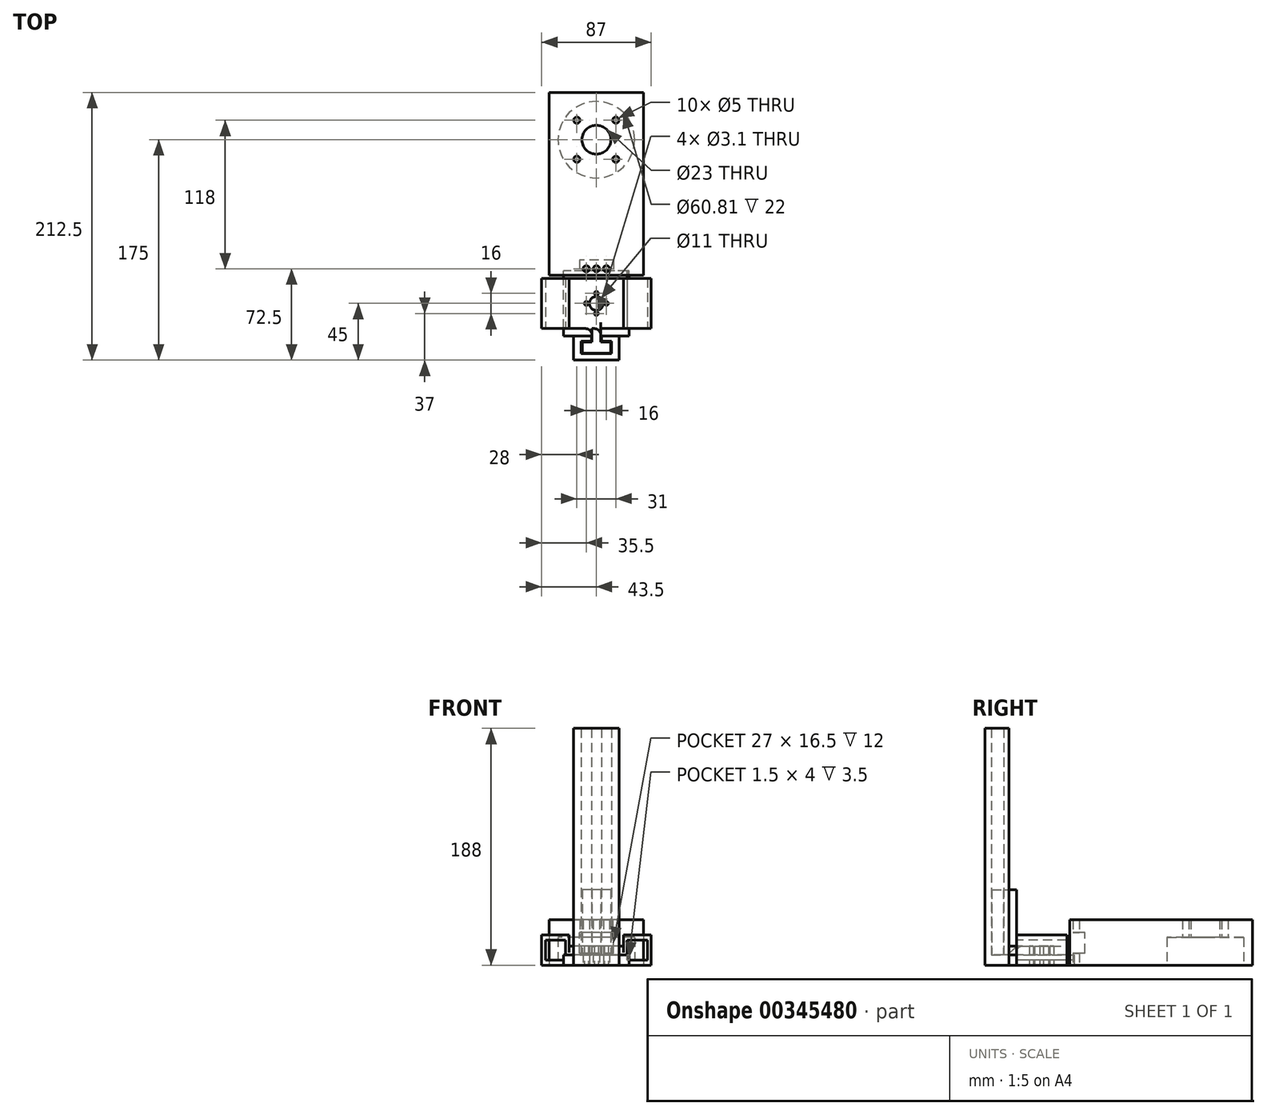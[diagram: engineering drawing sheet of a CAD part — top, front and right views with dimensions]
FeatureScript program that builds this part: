
annotation { "Feature Type Name" : "Feature", "Feature Type Description" : "" }
export const myFeature = defineFeature(function(context is Context, id is Id, definition is map)
    precondition{}
    {
        {
            var Q0;
            Q0=qCreatedBy(makeId("Top.planeOp"),FACE);
            var sketch = newSketch(context, id + "F0", { "sketchPlane" : qUnion([Q0])});
            skLineSegment(sketch, "E0.bottom", {"start": v(18, -10) * mm, "end": v(-18, -10) * mm});
            skLineSegment(sketch, "E0.top", {"start": v(18, 10) * mm, "end": v(4, 10) * mm});
            skLineSegment(sketch, "E0.left", {"start": v(18, -10) * mm, "end": v(18, 10) * mm});
            skLineSegment(sketch, "E0.right", {"start": v(-18, -10) * mm, "end": v(-18, 10) * mm});
            skPoint(sketch, "E0.middle", {"position": v(0, 0) * mm});
            skLineSegment(sketch, "E1.bottom", {"start": v(12, -5) * mm, "end": v(-12, -5) * mm});
            skLineSegment(sketch, "E1.top", {"start": v(12, 5) * mm, "end": v(4, 5) * mm});
            skLineSegment(sketch, "E1.left", {"start": v(12, -5) * mm, "end": v(12, 5) * mm});
            skLineSegment(sketch, "E1.right", {"start": v(-12, -5) * mm, "end": v(-12, 5) * mm});
            skPoint(sketch, "E2", {"position": v(-4, 10) * mm});
            skPoint(sketch, "E3.MirrorP", {"position": v(4, 10) * mm});
            skLineSegment(sketch, "E4", {"start": v(-4, 10) * mm, "end": v(-4, 5) * mm});
            skLineSegment(sketch, "E5", {"start": v(4, 10) * mm, "end": v(4, 5) * mm});
            skLineSegment(sketch, "E6.trimOffspring", {"start": v(-4, 10) * mm, "end": v(-18, 10) * mm});
            skLineSegment(sketch, "E7.trimOffspring", {"start": v(-4, 5) * mm, "end": v(-12, 5) * mm});
            skLineSegment(sketch, "E8.bottom", {"start": v(15.5, 19.5) * mm, "end": v(-15.5, 19.5) * mm, "construction": true});
            skLineSegment(sketch, "E8.top", {"start": v(15.5, 50.5) * mm, "end": v(-15.5, 50.5) * mm, "construction": true});
            skLineSegment(sketch, "E8.left", {"start": v(15.5, 19.5) * mm, "end": v(15.5, 50.5) * mm, "construction": true});
            skLineSegment(sketch, "E8.right", {"start": v(-15.5, 19.5) * mm, "end": v(-15.5, 50.5) * mm, "construction": true});
            skPoint(sketch, "E8.middle", {"position": v(0, 35) * mm});
            skCircle(sketch, "E9", {"center": v(15.5, 50.5) * mm, "radius": 2.5 * mm});
            skCircle(sketch, "E10", {"center": v(15.5, 19.5) * mm, "radius": 2.5 * mm});
            skCircle(sketch, "E11", {"center": v(-15.5, 19.5) * mm, "radius": 2.5 * mm});
            skCircle(sketch, "E12", {"center": v(-15.5, 50.5) * mm, "radius": 2.5 * mm});
            skLineSegment(sketch, "E13.bottom", {"start": v(26, 9) * mm, "end": v(-26, 9) * mm});
            skLineSegment(sketch, "E13.top", {"start": v(26, 61) * mm, "end": v(-26, 61) * mm});
            skLineSegment(sketch, "E13.left", {"start": v(26, 9) * mm, "end": v(26, 61) * mm});
            skLineSegment(sketch, "E13.right", {"start": v(-26, 9) * mm, "end": v(-26, 61) * mm});
            skCircle(sketch, "E14", {"center": v(0, 35) * mm, "radius": 11.5 * mm});
            skSolve(sketch);
        }
        {
            var Q0;
            Q0=makeQuery(id+"F0.imprint","IMPRINT",FACE,{"disambiguationData":[TD([[makeQuery(id+"F0.imprint","IMPRINT",EDGE,{"derivedFrom":sQuery(id+"F0.wireOp",EDGE,"E0.bottom")}),-1.0]])]});
            extrude(context, id + "F1", {"entities" : qUnion([Q0]), "depth" : 10 * mm});
        }
        {
            var Q0;
            Q0=qCreatedBy(makeId("Top.planeOp"),FACE);
            var sketch = newSketch(context, id + "F2", { "sketchPlane" : qUnion([Q0])});
            skLineSegment(sketch, "E15.bottom", {"start": v(11.25, -4.5) * mm, "end": v(-11.25, -4.5) * mm});
            skLineSegment(sketch, "E15.top", {"start": v(11.25, 4.5) * mm, "end": v(3.5, 4.5) * mm});
            skLineSegment(sketch, "E15.left", {"start": v(11.25, -4.5) * mm, "end": v(11.25, 4.5) * mm});
            skLineSegment(sketch, "E15.right", {"start": v(-11.25, -4.5) * mm, "end": v(-11.25, 4.5) * mm});
            skPoint(sketch, "E15.middle", {"position": v(0, 0) * mm});
            skLineSegment(sketch, "E16.top", {"start": v(3.5, 24.5) * mm, "end": v(-3.5, 24.5) * mm});
            skLineSegment(sketch, "E16.left", {"start": v(3.5, 4.5) * mm, "end": v(3.5, 24.5) * mm});
            skLineSegment(sketch, "E16.right", {"start": v(-3.5, 4.5) * mm, "end": v(-3.5, 24.5) * mm});
            skPoint(sketch, "E16.middle", {"position": v(0, 14.5) * mm});
            skLineSegment(sketch, "E17.trimOffspring", {"start": v(-3.5, 4.5) * mm, "end": v(-11.25, 4.5) * mm});
            skPoint(sketch, "E18.0", {"position": v(0, 35) * mm});
            skCircle(sketch, "E19", {"center": v(0, 35) * mm, "radius": 5.5 * mm});
            skCircle(sketch, "E20", {"center": v(0, 35) * mm, "radius": 8 * mm, "construction": true});
            skCircle(sketch, "E21", {"center": v(0, 43) * mm, "radius": 1.55 * mm});
            skCircle(sketch, "E22.1.0", {"center": v(-8, 35) * mm, "radius": 1.55 * mm});
            skCircle(sketch, "E22.2.0", {"center": v(0, 27) * mm, "radius": 1.55 * mm});
            skCircle(sketch, "E22.3.0", {"center": v(8, 35) * mm, "radius": 1.55 * mm});
            skLineSegment(sketch, "E23.bottom", {"start": v(21.5, 15) * mm, "end": v(-21.5, 15) * mm});
            skLineSegment(sketch, "E23.top", {"start": v(21.5, 55) * mm, "end": v(-21.5, 55) * mm});
            skLineSegment(sketch, "E23.left", {"start": v(21.5, 15) * mm, "end": v(21.5, 55) * mm});
            skLineSegment(sketch, "E23.right", {"start": v(-21.5, 15) * mm, "end": v(-21.5, 55) * mm});
            skLineSegment(sketch, "E24.bottom", {"start": v(-21.5, 55) * mm, "end": v(21.5, 55) * mm});
            skPoint(sketch, "E25.orphan", {"position": v(-21.5, 60) * mm});
            skPoint(sketch, "E26.center.orphan", {"position": v(-8, 60) * mm});
            skPoint(sketch, "E27.center.orphan", {"position": v(8, 60) * mm});
            skPoint(sketch, "E28.center.orphan", {"position": v(0, 60) * mm});
            skPoint(sketch, "E29.orphan", {"position": v(21.5, 60) * mm});
            skPoint(sketch, "E24.top.start.orphan", {"position": v(-21.5, 65) * mm});
            skPoint(sketch, "E30.orphan", {"position": v(21.5, 65) * mm});
            skLineSegment(sketch, "E31.bottom", {"start": v(21.5, 15) * mm, "end": v(43.5, 15) * mm});
            skLineSegment(sketch, "E31.top", {"start": v(21.5, 55) * mm, "end": v(43.5, 55) * mm});
            skLineSegment(sketch, "E31.right", {"start": v(43.5, 15) * mm, "end": v(43.5, 55) * mm});
            skLineSegment(sketch, "E32.MirrorCS", {"start": v(-43.5, 15) * mm, "end": v(-43.5, 55) * mm});
            skLineSegment(sketch, "E33.MirrorCS", {"start": v(-21.5, 15) * mm, "end": v(-43.5, 15) * mm});
            skLineSegment(sketch, "E34.MirrorCS", {"start": v(-21.5, 55) * mm, "end": v(-43.5, 55) * mm});
            skSolve(sketch);
        }
        {
            var Q0;
            Q0=makeQuery(id+"F2.imprint","IMPRINT",FACE,{"disambiguationData":[TD([[makeQuery(id+"F2.imprint","IMPRINT",EDGE,{"derivedFrom":sQuery(id+"F2.wireOp",EDGE,"E15.bottom")}),-1.0]])]});
            extrude(context, id + "F3", {"entities" : qUnion([Q0]), "depth" : 5 * mm});
        }
        {
            var Q0;
            {var subQ5=sQuery(id+"F0.wireOp",EDGE,"E0.bottom");Q0=makeQuery(id+"F0.imprint","IMPRINT",FACE,{"disambiguationData":[TD([[makeQuery(id+"F0.imprint","IMPRINT",EDGE,{"derivedFrom":subQ5}),-1.0]])]});}
            extrude(context, id + "F4", {"entities" : qUnion([Q0]), "depth" : 188 * mm});
        }
        {
            var Q0;
            {var subQ1=sQuery(id+"F0.wireOp",EDGE,"E0.top");Q0=makeQuery(id+"F0.imprint","IMPRINT",FACE,{"disambiguationData":[TD([[makeQuery(id+"F0.imprint","IMPRINT",EDGE,{"derivedFrom":subQ1}),-1.0]])]});}
            extrude(context, id + "F5", {"entities" : qUnion([Q0]), "operationType" : NewBodyOperationType.ADD, "depth" : 8 * mm});
        }
        {
            var Q0;
            Q0=makeQuery(id+"F5.opExtrude","SWEPT_BODY",BODY,{"disambiguationData":[OSD([sQuery(id+"F0.wireOp",EDGE,"E0.top"),sQuery(id+"F0.wireOp",EDGE,"E0.left"),sQuery(id+"F0.wireOp",EDGE,"E0.right"),sQuery(id+"F0.wireOp",EDGE,"E4"),sQuery(id+"F0.wireOp",EDGE,"E5"),sQuery(id+"F0.wireOp",EDGE,"E6.trimOffspring"),sQuery(id+"F0.wireOp",EDGE,"E9"),sQuery(id+"F0.wireOp",EDGE,"E10"),sQuery(id+"F0.wireOp",EDGE,"E11"),sQuery(id+"F0.wireOp",EDGE,"E12"),sQuery(id+"F0.wireOp",EDGE,"E13.bottom"),sQuery(id+"F0.wireOp",EDGE,"E13.top"),sQuery(id+"F0.wireOp",EDGE,"E13.left"),sQuery(id+"F0.wireOp",EDGE,"E13.right"),sQuery(id+"F0.wireOp",EDGE,"E14")])]});
            deleteBodies(context, id + "F6", {"entities" : qUnion([Q0])});
        }
        {
            var Q0;
            Q0=makeQuery(id+"F0.imprint","IMPRINT",FACE,{"disambiguationData":[TD([[makeQuery(id+"F0.imprint","IMPRINT",EDGE,{"derivedFrom":sQuery(id+"F0.wireOp",EDGE,"E1.bottom")}),-1.0]])]});
            var Q1;
            {var subQ1=sQuery(id+"F0.wireOp",EDGE,"E0.top");Q1=makeQuery(id+"F0.imprint","IMPRINT",FACE,{"disambiguationData":[TD([[makeQuery(id+"F0.imprint","IMPRINT",EDGE,{"derivedFrom":subQ1}),-1.0]])]});}
            var Q2;
            {var subQ5=sQuery(id+"F0.wireOp",EDGE,"E0.bottom");Q2=makeQuery(id+"F0.imprint","IMPRINT",FACE,{"disambiguationData":[TD([[makeQuery(id+"F0.imprint","IMPRINT",EDGE,{"derivedFrom":subQ5}),-1.0]])]});}
            var Q3;
            {var subQ0=sQuery(id+"F0.wireOp",EDGE,"E0.top");Q3=makeQuery(id+"F0.imprint","IMPRINT",FACE,{"disambiguationData":[TD([[makeQuery(id+"F0.imprint","IMPRINT",EDGE,{"derivedFrom":subQ0}),1.0]])]});}
            var Q4;
            {var subQ0=sQuery(id+"F0.wireOp",EDGE,"E6.trimOffspring");Q4=makeQuery(id+"F0.imprint","IMPRINT",FACE,{"disambiguationData":[TD([[makeQuery(id+"F0.imprint","IMPRINT",EDGE,{"derivedFrom":subQ0}),1.0]])]});}
            extrude(context, id + "F7", {"entities" : qUnion([Q0, Q1, Q2, Q3, Q4]), "operationType" : NewBodyOperationType.ADD, "depth" : 8 * mm});
        }
        {
            var Q0;
            Q0=makeQuery(id+"F2.imprint","IMPRINT",FACE,{"disambiguationData":[TD([[makeQuery(id+"F2.imprint","IMPRINT",EDGE,{"derivedFrom":sQuery(id+"F2.wireOp",EDGE,"E15.bottom")}),-1.0]])]});
            extrude(context, id + "F8", {"entities" : qUnion([Q0]), "depth" : 60 * mm});
        }
        {
            var Q0;
            {var subQ4=sQuery(id+"F2.wireOp",EDGE,"E16.top");Q0=makeQuery(id+"F2.imprint","IMPRINT",FACE,{"disambiguationData":[TD([[makeQuery(id+"F2.imprint","IMPRINT",EDGE,{"derivedFrom":subQ4}),-1.0]])]});}
            var Q1;
            {var subQ0=sQuery(id+"F2.wireOp",EDGE,"E16.top");Q1=makeQuery(id+"F2.imprint","IMPRINT",FACE,{"disambiguationData":[TD([[makeQuery(id+"F2.imprint","IMPRINT",EDGE,{"derivedFrom":subQ0}),1.0]])]});}
            var Q2;
            Q2=makeQuery(id+"F2.imprint","IMPRINT",FACE,{"disambiguationData":[TD([[makeQuery(id+"F2.imprint","IMPRINT",EDGE,{"derivedFrom":sQuery(id+"F2.wireOp",EDGE,"E24.bottom")}),1.0]])]});
            extrude(context, id + "F9", {"entities" : qUnion([Q0, Q1, Q2]), "operationType" : NewBodyOperationType.ADD, "depth" : 15 * mm});
        }
        {
            var Q0;
            {var subQ0=sQuery(id+"F2.wireOp",EDGE,"E16.right");var subQ1=sQuery(id+"F2.wireOp",EDGE,"E23.bottom");Q0=makeQuery(id+"F9.boolean.opBoolean","SPLIT",EDGE,{"disambiguationData":[topologyDisambiguationEdgeConnected([makeQuery(id+"F9.opExtrude","SWEPT_FACE",FACE,{"disambiguationData":[OSD([subQ1])]})])],"derivedFrom":makeQuery(id+"F8.opExtrude","SWEPT_EDGE",EDGE,{"disambiguationData":[OSD([subQ0,subQ1])]})});}
            var Q1;
            {var subQ0=sQuery(id+"F2.wireOp",EDGE,"E16.left");var subQ1=sQuery(id+"F2.wireOp",EDGE,"E23.bottom");Q1=makeQuery(id+"F9.boolean.opBoolean","SPLIT",EDGE,{"disambiguationData":[topologyDisambiguationEdgeConnected([makeQuery(id+"F9.opExtrude","SWEPT_FACE",FACE,{"disambiguationData":[OSD([subQ1])]})])],"derivedFrom":makeQuery(id+"F8.opExtrude","SWEPT_EDGE",EDGE,{"disambiguationData":[OSD([subQ0,subQ1])]})});}
            fillet(context, id + "F10", {"entities" : qUnion([Q0, Q1]), "radius" : 5 * mm, "tangentPropagation" : true, "allowEdgeOverflow" : false});
        }
        {
            var Q0;
            {var subQ0=sQuery(id+"F2.wireOp",EDGE,"E23.bottom");Q0=makeQuery(id+"F9.boolean.opBoolean","SPLIT",EDGE,{"disambiguationData":[topologyDisambiguationEdgeConnected([makeQuery(id+"F8.opExtrude","SWEPT_FACE",FACE,{"disambiguationData":[OSD([subQ0])]}),makeQuery(id+"F9.opExtrude","CAP_FACE",FACE,{"disambiguationData":[OSD([sQuery(id+"F2.wireOp",EDGE,"E19"),sQuery(id+"F2.wireOp",EDGE,"E21"),sQuery(id+"F2.wireOp",EDGE,"E22.1.0"),sQuery(id+"F2.wireOp",EDGE,"E22.2.0"),sQuery(id+"F2.wireOp",EDGE,"E22.3.0"),subQ0,sQuery(id+"F2.wireOp",EDGE,"E23.left"),sQuery(id+"F2.wireOp",EDGE,"E23.right"),sQuery(id+"F2.wireOp",EDGE,"E24.top"),sQuery(id+"F2.wireOp",EDGE,"E24.left"),sQuery(id+"F2.wireOp",EDGE,"E24.right"),sQuery(id+"F2.wireOp",EDGE,"E28"),sQuery(id+"F2.wireOp",EDGE,"E27"),sQuery(id+"F2.wireOp",EDGE,"E26")])],"isStart":false})])],"derivedFrom":makeQuery(id+"F9.opExtrude","CAP_EDGE",EDGE,{"disambiguationData":[OSD([subQ0])],"isStart":false})});}
            fillet(context, id + "F11", {"entities" : qUnion([Q0]), "radius" : 5 * mm, "tangentPropagation" : true, "allowEdgeOverflow" : false});
        }
        {
            var Q0;
            Q0=qCreatedBy(makeId("Top.planeOp"),FACE);
            var sketch = newSketch(context, id + "F12", { "sketchPlane" : qUnion([Q0])});
            skPoint(sketch, "E35", {"position": v(0, 165) * mm});
            skLineSegment(sketch, "E36.bottom", {"start": v(15.5, 149.5) * mm, "end": v(-15.5, 149.5) * mm, "construction": true});
            skLineSegment(sketch, "E36.top", {"start": v(15.5, 180.5) * mm, "end": v(-15.5, 180.5) * mm, "construction": true});
            skLineSegment(sketch, "E36.left", {"start": v(15.5, 149.5) * mm, "end": v(15.5, 180.5) * mm, "construction": true});
            skLineSegment(sketch, "E36.right", {"start": v(-15.5, 149.5) * mm, "end": v(-15.5, 180.5) * mm, "construction": true});
            skCircle(sketch, "E37", {"center": v(15.5, 180.5) * mm, "radius": 2.5 * mm});
            skCircle(sketch, "E38", {"center": v(15.5, 149.5) * mm, "radius": 2.5 * mm});
            skCircle(sketch, "E39", {"center": v(-15.5, 149.5) * mm, "radius": 2.5 * mm});
            skCircle(sketch, "E40", {"center": v(-15.5, 180.5) * mm, "radius": 2.5 * mm});
            skCircle(sketch, "E41", {"center": v(0, 165) * mm, "radius": 11.5 * mm});
            skLineSegment(sketch, "E42.bottom", {"start": v(21.5, 143.5) * mm, "end": v(-21.5, 143.5) * mm, "construction": true});
            skLineSegment(sketch, "E42.top", {"start": v(21.5, 186.5) * mm, "end": v(-21.5, 186.5) * mm, "construction": true});
            skLineSegment(sketch, "E42.left", {"start": v(21.5, 143.5) * mm, "end": v(21.5, 186.5) * mm, "construction": true});
            skLineSegment(sketch, "E42.right", {"start": v(-21.5, 143.5) * mm, "end": v(-21.5, 186.5) * mm, "construction": true});
            skLineSegment(sketch, "E43.bottom", {"start": v(37.5, 127.5) * mm, "end": v(-37.5, 127.5) * mm});
            skLineSegment(sketch, "E43.top", {"start": v(37.5, 202.5) * mm, "end": v(-37.5, 202.5) * mm});
            skLineSegment(sketch, "E43.left", {"start": v(37.5, 127.5) * mm, "end": v(37.5, 202.5) * mm});
            skLineSegment(sketch, "E43.right", {"start": v(-37.5, 127.5) * mm, "end": v(-37.5, 202.5) * mm});
            skLineSegment(sketch, "E44", {"start": v(-37.5, 127.5) * mm, "end": v(-37.5, 57.5) * mm});
            skLineSegment(sketch, "E45", {"start": v(-37.5, 57.5) * mm, "end": v(37.5, 57.5) * mm});
            skLineSegment(sketch, "E46", {"start": v(37.5, 57.5) * mm, "end": v(37.5, 127.5) * mm});
            skPoint(sketch, "E47", {"position": v(0, 62.5) * mm});
            skPoint(sketch, "E47.positionSnap0", {"position": v(0, 57.5) * mm});
            skPoint(sketch, "E48", {"position": v(8, 62.5) * mm});
            skCircle(sketch, "E49", {"center": v(0, 62.5) * mm, "radius": 2.5 * mm});
            skCircle(sketch, "E50", {"center": v(8, 62.5) * mm, "radius": 2.5 * mm});
            skCircle(sketch, "E51.MirrorC", {"center": v(-8, 62.5) * mm, "radius": 2.5 * mm});
            skCircle(sketch, "E52", {"center": v(0, 165) * mm, "radius": 30.4 * mm});
            skSolve(sketch);
        }
        {
            var Q0;
            Q0=makeQuery(id+"F12.imprint","IMPRINT",FACE,{"disambiguationData":[TD([[makeQuery(id+"F12.imprint","IMPRINT",EDGE,{"derivedFrom":sQuery(id+"F12.wireOp",EDGE,"E43.bottom")}),1.0]])]});
            var Q1;
            Q1=makeQuery(id+"F12.imprint","IMPRINT",FACE,{"disambiguationData":[TD([[makeQuery(id+"F12.imprint","IMPRINT",EDGE,{"derivedFrom":sQuery(id+"F12.wireOp",EDGE,"E43.bottom")}),-1.0]])]});
            var Q2;
            Q2=makeQuery(id+"F12.imprint","IMPRINT",FACE,{"disambiguationData":[TD([[makeQuery(id+"F12.imprint","IMPRINT",EDGE,{"derivedFrom":sQuery(id+"F12.wireOp",EDGE,"E37")}),-1.0]])]});
            extrude(context, id + "F13", {"entities" : qUnion([Q0, Q1, Q2]), "depth" : 36 * mm});
        }
        {
            var Q0;
            Q0=makeQuery(id+"F12.imprint","IMPRINT",FACE,{"disambiguationData":[TD([[makeQuery(id+"F12.imprint","IMPRINT",EDGE,{"derivedFrom":sQuery(id+"F12.wireOp",EDGE,"E37")}),-1.0]])]});
            extrude(context, id + "F14", {"entities" : qUnion([Q0]), "operationType" : NewBodyOperationType.REMOVE, "depth" : 22 * mm});
        }
        {
            var Q0;
            Q0=makeQuery(id+"F13.opExtrude","SWEPT_FACE",FACE,{"disambiguationData":[OSD([sQuery(id+"F12.wireOp",EDGE,"E45")])]});
            var sketch = newSketch(context, id + "F15", { "sketchPlane" : qUnion([Q0])});
            skLineSegment(sketch, "E53", {"start": v(0, 9.5) * mm, "end": v(-13.5, 9.5) * mm});
            skLineSegment(sketch, "E54", {"start": v(-13.5, 9.5) * mm, "end": v(-13.5, 26) * mm});
            skLineSegment(sketch, "E55", {"start": v(-13.5, 26) * mm, "end": v(0, 26) * mm});
            skLineSegment(sketch, "E56.MirrorCS", {"start": v(13.5, 9.5) * mm, "end": v(13.5, 26) * mm});
            skLineSegment(sketch, "E57.MirrorCS", {"start": v(0, 9.5) * mm, "end": v(13.5, 9.5) * mm});
            skLineSegment(sketch, "E58.MirrorCS", {"start": v(13.5, 26) * mm, "end": v(0, 26) * mm});
            skSolve(sketch);
        }
        {
            var Q0;
            Q0=makeQuery(id+"F15.imprint","IMPRINT",FACE,{"disambiguationData":[TD([[makeQuery(id+"F15.imprint","IMPRINT",EDGE,{"derivedFrom":sQuery(id+"F15.wireOp",EDGE,"E53")}),-1.0]])]});
            extrude(context, id + "F16", {"entities" : qUnion([Q0]), "operationType" : NewBodyOperationType.REMOVE, "oppositeDirection" : true, "depth" : 12 * mm});
        }
        {
            var Q0;
            Q0=makeQuery(id+"F2.imprint","IMPRINT",FACE,{"disambiguationData":[TD([[makeQuery(id+"F2.imprint","IMPRINT",EDGE,{"derivedFrom":sQuery(id+"F2.wireOp",EDGE,"E23.right")}),1.0]])]});
            var Q1;
            Q1=makeQuery(id+"F2.imprint","IMPRINT",FACE,{"disambiguationData":[TD([[makeQuery(id+"F2.imprint","IMPRINT",EDGE,{"derivedFrom":sQuery(id+"F2.wireOp",EDGE,"E31.bottom")}),1.0]])]});
            extrude(context, id + "F17", {"entities" : qUnion([Q0, Q1]), "operationType" : NewBodyOperationType.ADD, "depth" : 24 * mm});
        }
        {
            var Q0;
            {var subQ0=sQuery(id+"F2.wireOp",EDGE,"E23.bottom");var subQ9=sQuery(id+"F2.wireOp",EDGE,"E16.right");Q0=makeQuery(id+"F17.boolean.opBoolean","MERGE",FACE,{"derivedFrom":[makeQuery(id+"F9.boolean.opBoolean","SPLIT",FACE,{"disambiguationData":[TD([makeQuery(id+"F8.opExtrude","SWEPT_FACE",FACE,{"disambiguationData":[OSD([subQ9])]})])],"derivedFrom":makeQuery(id+"F9.opExtrude","SWEPT_FACE",FACE,{"disambiguationData":[OSD([subQ0])]})}),makeQuery(id+"F17.opExtrude","SWEPT_FACE",FACE,{"disambiguationData":[OSD([sQuery(id+"F2.wireOp",EDGE,"E33.MirrorCS")])]})]});}
            var sketch = newSketch(context, id + "F18", { "sketchPlane" : qUnion([Q0])});
            skLineSegment(sketch, "E59.bottom", {"start": v(-40.5, 20) * mm, "end": v(-24.5, 20) * mm});
            skLineSegment(sketch, "E59.top", {"start": v(-40.5, 4) * mm, "end": v(-24.5, 4) * mm});
            skLineSegment(sketch, "E59.left", {"start": v(-40.5, 20) * mm, "end": v(-40.5, 4) * mm});
            skLineSegment(sketch, "E59.right", {"start": v(-24.5, 20) * mm, "end": v(-24.5, 4) * mm});
            skLineSegment(sketch, "E60.MirrorCS", {"start": v(40.5, 4) * mm, "end": v(24.5, 4) * mm});
            skLineSegment(sketch, "E61.MirrorCS", {"start": v(24.5, 20) * mm, "end": v(24.5, 4) * mm});
            skLineSegment(sketch, "E62.MirrorCS", {"start": v(40.5, 20) * mm, "end": v(24.5, 20) * mm});
            skLineSegment(sketch, "E63.MirrorCS", {"start": v(40.5, 20) * mm, "end": v(40.5, 4) * mm});
            skSolve(sketch);
        }
        {
            var Q0;
            Q0=makeQuery(id+"F18.imprint","IMPRINT",FACE,{"disambiguationData":[TD([[makeQuery(id+"F18.imprint","IMPRINT",EDGE,{"derivedFrom":sQuery(id+"F18.wireOp",EDGE,"E59.bottom")}),-1.0]])]});
            var Q1;
            Q1=makeQuery(id+"F18.imprint","IMPRINT",FACE,{"disambiguationData":[TD([[makeQuery(id+"F18.imprint","IMPRINT",EDGE,{"derivedFrom":sQuery(id+"F18.wireOp",EDGE,"E60.MirrorCS")}),-1.0]])]});
            extrude(context, id + "F19", {"entities" : qUnion([Q0, Q1]), "operationType" : NewBodyOperationType.REMOVE, "endBound" : BoundingType.UP_TO_NEXT, "oppositeDirection" : true, "depth" : 25 * mm});
        }
    });
